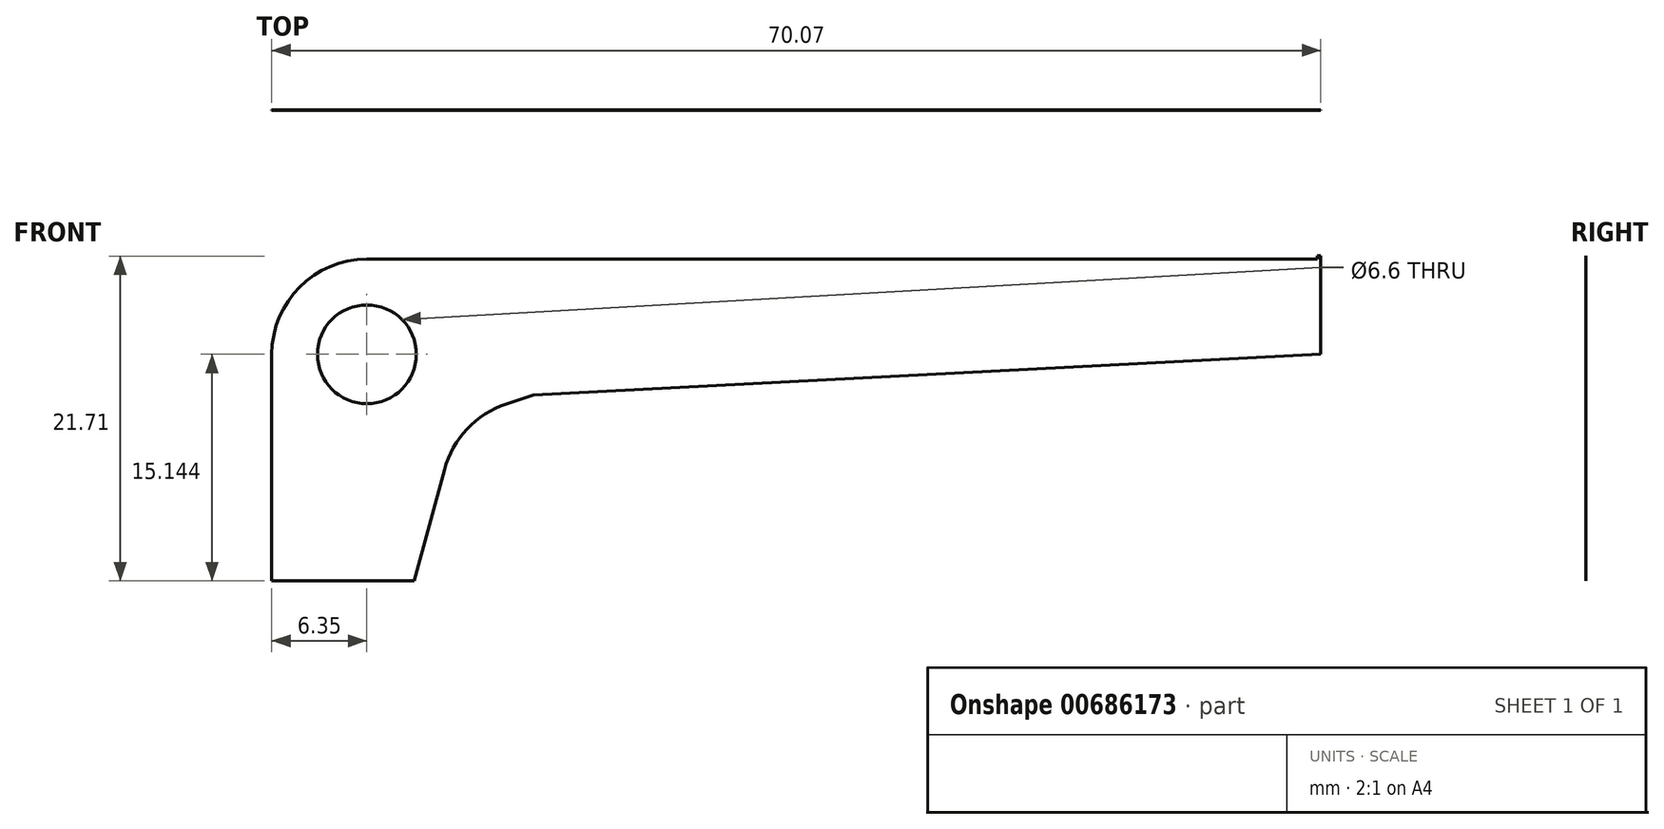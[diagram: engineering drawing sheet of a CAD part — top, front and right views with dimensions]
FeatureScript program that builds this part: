
annotation { "Feature Type Name" : "Feature", "Feature Type Description" : "" }
export const myFeature = defineFeature(function(context is Context, id is Id, definition is map)
    precondition{}
    {
        {
            var Q0;
            Q0=qCreatedBy(makeId("Front.planeOp"),FACE);
            var sketch = newSketch(context, id + "F0", { "sketchPlane" : qUnion([Q0])});
            skLineSegment(sketch, "E0.top", {"start": v(6.35, 21.5) * mm, "end": v(69.85, 21.5) * mm});
            skLineSegment(sketch, "E0.left", {"start": v(0, 0) * mm, "end": v(0, 15.14) * mm});
            skLineSegment(sketch, "E1.bottom", {"start": v(70.07, 21.71) * mm, "end": v(69.85, 21.71) * mm});
            skLineSegment(sketch, "E1.top", {"start": v(70.07, 15.14) * mm, "end": v(69.85, 15.14) * mm});
            skLineSegment(sketch, "E1.left", {"start": v(70.07, 21.71) * mm, "end": v(70.07, 15.14) * mm});
            skLineSegment(sketch, "E1.right", {"start": v(69.85, 21.71) * mm, "end": v(69.85, 15.14) * mm});
            skLineSegment(sketch, "E2", {"start": v(11.53, 7.44) * mm, "end": v(9.52, 0) * mm});
            skPoint(sketch, "E2.startSnap0", {"position": v(0, 10.75) * mm});
            skLineSegment(sketch, "E3", {"start": v(17.5, 12.42) * mm, "end": v(70.07, 15.14) * mm});
            skLineSegment(sketch, "E4", {"start": v(15.67, 11.82) * mm, "end": v(17.5, 12.42) * mm});
            skLineSegment(sketch, "E5", {"start": v(9.52, 0) * mm, "end": v(0, 0) * mm});
            skPoint(sketch, "E6.visualSharp", {"position": v(0, 21.5) * mm});
            skArc(sketch, "E6.filletArc", {"start": v(6.35, 21.5) * mm, "mid": v(1.86, 19.63) * mm, "end": v(0, 15.14) * mm});
            skPoint(sketch, "E7.visualSharp", {"position": v(12.42, 10.75) * mm});
            skArc(sketch, "E7.filletArc", {"start": v(15.67, 11.82) * mm, "mid": v(13.05, 10.15) * mm, "end": v(11.53, 7.44) * mm});
            skSolve(sketch);
        }
        {
            var Q0;
            Q0 = qSketchRegion(id + "F0", true);
            extrude(context, id + "F1", {"entities" : qUnion([Q0]), "depth" : 3 / 812.8 * mm, "offsetDistance" : 25.4 * mm});
        }
        {
            var Q0;
            Q0=makeQuery(id+"F1.opExtrude","CAP_FACE",FACE,{"disambiguationData":[OSD([sQuery(id+"F0.wireOp",EDGE,"E0.top"),sQuery(id+"F0.wireOp",EDGE,"E0.left"),sQuery(id+"F0.wireOp",EDGE,"E1.bottom"),sQuery(id+"F0.wireOp",EDGE,"E1.left"),sQuery(id+"F0.wireOp",EDGE,"E1.right"),sQuery(id+"F0.wireOp",EDGE,"E2"),sQuery(id+"F0.wireOp",EDGE,"E3"),sQuery(id+"F0.wireOp",EDGE,"E4"),sQuery(id+"F0.wireOp",EDGE,"E5"),sQuery(id+"F0.wireOp",EDGE,"E6.filletArc"),sQuery(id+"F0.wireOp",EDGE,"E7.filletArc")])],"isStart":false});
            var sketch = newSketch(context, id + "F2", { "sketchPlane" : qUnion([Q0])});
            skCircle(sketch, "E8", {"center": v(6.35, 15.14) * mm, "radius": 3.3 * mm});
            skSolve(sketch);
        }
        {
            var Q0;
            Q0 = qSketchRegion(id + "F2", true);
            extrude(context, id + "F3", {"entities" : qUnion([Q0]), "operationType" : NewBodyOperationType.REMOVE, "oppositeDirection" : true, "depth" : 25.4 * mm, "offsetDistance" : 25.4 * mm});
        }
    });
